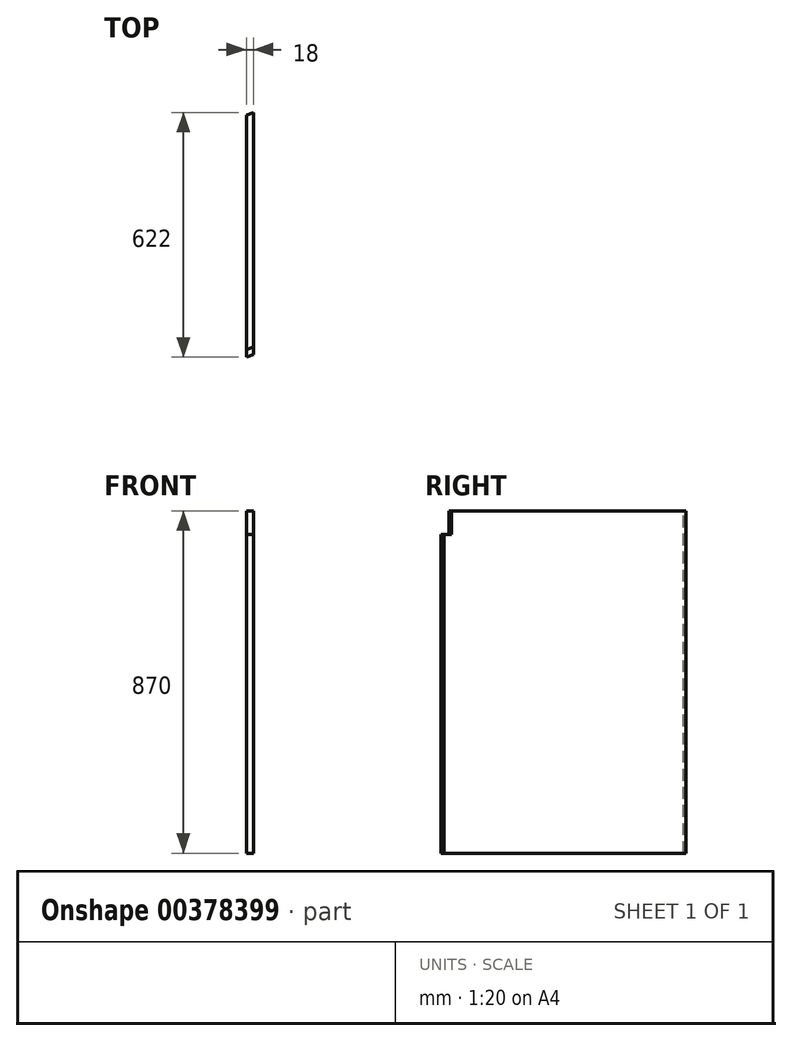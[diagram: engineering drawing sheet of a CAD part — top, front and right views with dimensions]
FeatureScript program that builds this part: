
annotation { "Feature Type Name" : "Feature", "Feature Type Description" : "" }
export const myFeature = defineFeature(function(context is Context, id is Id, definition is map)
    precondition{}
    {
        {
            var Q0;
            Q0=qCreatedBy(makeId("Right.planeOp"),FACE);
            var sketch = newSketch(context, id + "F0", { "sketchPlane" : qUnion([Q0])});
            skLineSegment(sketch, "E0.bottom", {"start": v(311, 435) * mm, "end": v(-311, 435) * mm});
            skLineSegment(sketch, "E0.top", {"start": v(311, -435) * mm, "end": v(-311, -435) * mm});
            skLineSegment(sketch, "E0.left", {"start": v(311, 435) * mm, "end": v(311, -435) * mm});
            skLineSegment(sketch, "E0.right", {"start": v(-311, 435) * mm, "end": v(-311, -435) * mm});
            skPoint(sketch, "E0.middle", {"position": v(0, 0) * mm});
            skSolve(sketch);
        }
        {
            var Q0;
            Q0 = qSketchRegion(id + "F0", true);
            extrude(context, id + "F1", {"entities" : qUnion([Q0]), "depth" : 18 * mm});
        }
        {
            var Q0;
            Q0=makeQuery(id+"F1.opExtrude","SWEPT_FACE",FACE,{"disambiguationData":[OSD([sQuery(id+"F0.wireOp",EDGE,"E0.bottom")])]});
            var sketch = newSketch(context, id + "F2", { "sketchPlane" : qUnion([Q0])});
            skLineSegment(sketch, "E1", {"start": v(18, 311) * mm, "end": v(0, 311) * mm});
            skLineSegment(sketch, "E2", {"start": v(0, 311) * mm, "end": v(0, 304.1) * mm});
            skLineSegment(sketch, "E3", {"start": v(0, 304.1) * mm, "end": v(18, 311) * mm});
            skLineSegment(sketch, "E4", {"start": v(0, -311) * mm, "end": v(18, -311) * mm});
            skLineSegment(sketch, "E5", {"start": v(18, -311) * mm, "end": v(18, -304.1) * mm});
            skLineSegment(sketch, "E6", {"start": v(18, -304.1) * mm, "end": v(0, -311) * mm});
            skSolve(sketch);
        }
        {
            var Q0;
            Q0 = qSketchRegion(id + "F2", true);
            extrude(context, id + "F3", {"entities" : qUnion([Q0]), "operationType" : NewBodyOperationType.REMOVE, "oppositeDirection" : true, "depth" : 870 * mm});
        }
        {
            var Q0;
            Q0=makeQuery(id+"F1.opExtrude","SWEPT_FACE",FACE,{"disambiguationData":[OSD([sQuery(id+"F0.wireOp",EDGE,"E0.bottom")])]});
            var sketch = newSketch(context, id + "F4", { "sketchPlane" : qUnion([Q0])});
            skLineSegment(sketch, "E7", {"start": v(0, -311) * mm, "end": v(0, -291.72) * mm});
            skLineSegment(sketch, "E8", {"start": v(0, -291.72) * mm, "end": v(18, -284.8) * mm});
            skLineSegment(sketch, "E9", {"start": v(18, -284.8) * mm, "end": v(18, -304.1) * mm});
            skLineSegment(sketch, "E10", {"start": v(18, -304.1) * mm, "end": v(0, -311) * mm});
            skSolve(sketch);
        }
        {
            var Q0;
            Q0=makeQuery(id+"F4.imprint","IMPRINT",FACE,{"disambiguationData":[TD([[makeQuery(id+"F4.imprint","IMPRINT",EDGE,{"derivedFrom":sQuery(id+"F4.wireOp",EDGE,"E7")}),1.0]])]});
            extrude(context, id + "F5", {"entities" : qUnion([Q0]), "operationType" : NewBodyOperationType.REMOVE, "oppositeDirection" : true, "depth" : 60 * mm});
        }
    });
